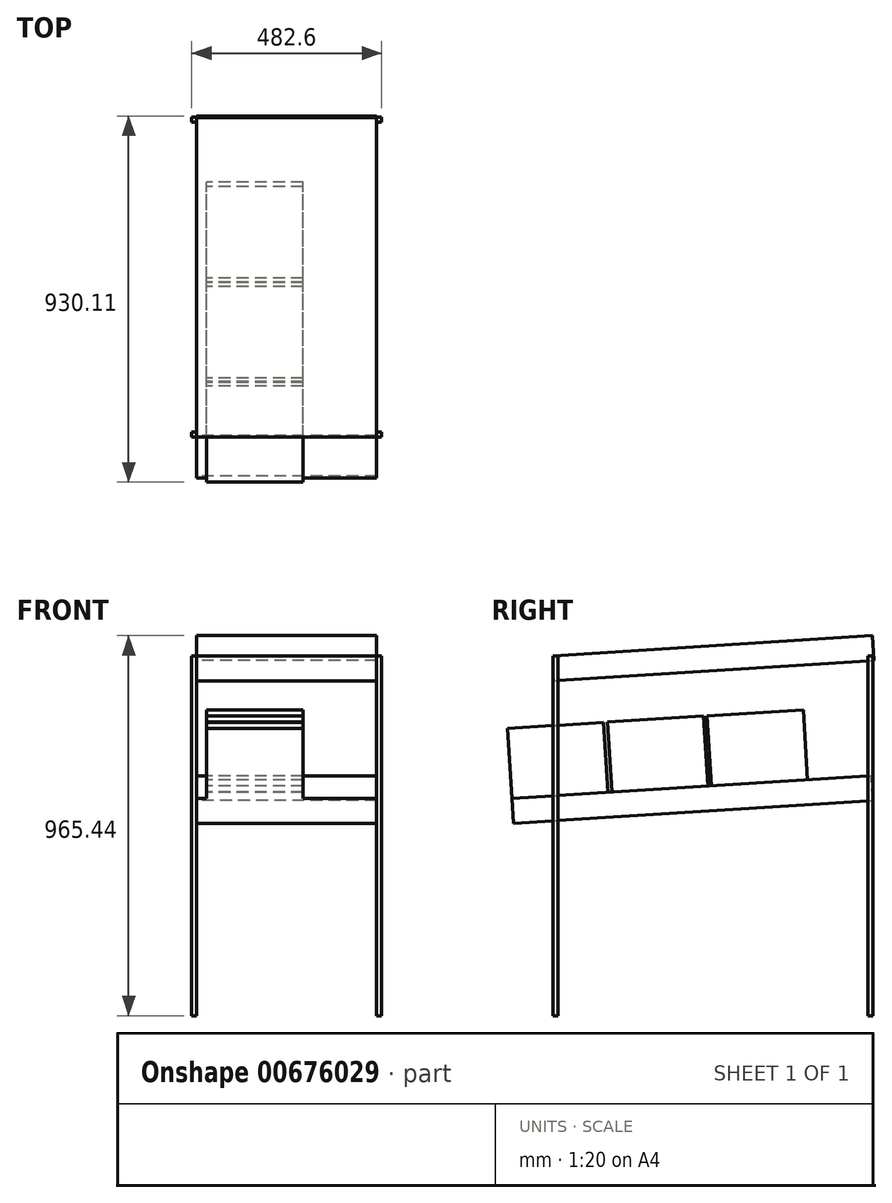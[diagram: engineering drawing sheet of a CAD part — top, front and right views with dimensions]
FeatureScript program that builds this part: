
annotation { "Feature Type Name" : "Feature", "Feature Type Description" : "" }
export const myFeature = defineFeature(function(context is Context, id is Id, definition is map)
    precondition{}
    {
        {
            var Q0;
            Q0=qCreatedBy(makeId("Top.planeOp"),FACE);
            cPlane(context, id + "F0", {"entities" : qUnion([Q0]), "cplaneType" : CPlaneType.OFFSET, "offset" : 558.8 * mm, "width" : 152.4 * mm, "height" : 152.4 * mm});
        }
        {
            var Q0;
            Q0=qCreatedBy(makeId("Top.planeOp"),FACE);
            cPlane(context, id + "F1", {"entities" : qUnion([Q0]), "cplaneType" : CPlaneType.OFFSET, "offset" : 914.4 * mm, "width" : 152.4 * mm, "height" : 152.4 * mm});
        }
        {
            var Q0;
            Q0=qCreatedBy(makeId("Top.planeOp"),FACE);
            var sketch = newSketch(context, id + "F2", { "sketchPlane" : qUnion([Q0])});
            skLineSegment(sketch, "E0.bottom", {"start": v(-228.6, 0) * mm, "end": v(-241.3, 0) * mm});
            skLineSegment(sketch, "E0.top", {"start": v(-228.6, 12.7) * mm, "end": v(-241.3, 12.7) * mm});
            skLineSegment(sketch, "E0.left", {"start": v(-228.6, 0) * mm, "end": v(-228.6, 12.7) * mm});
            skLineSegment(sketch, "E0.right", {"start": v(-241.3, 0) * mm, "end": v(-241.3, 12.7) * mm});
            skLineSegment(sketch, "E1.bottom", {"start": v(228.6, 0) * mm, "end": v(241.3, 0) * mm});
            skLineSegment(sketch, "E1.top", {"start": v(228.6, 12.7) * mm, "end": v(241.3, 12.7) * mm});
            skLineSegment(sketch, "E1.left", {"start": v(228.6, 0) * mm, "end": v(228.6, 12.7) * mm});
            skLineSegment(sketch, "E1.right", {"start": v(241.3, 0) * mm, "end": v(241.3, 12.7) * mm});
            skLineSegment(sketch, "E2.bottom", {"start": v(228.6, 800.1) * mm, "end": v(241.3, 800.1) * mm});
            skLineSegment(sketch, "E2.top", {"start": v(228.6, 812.8) * mm, "end": v(241.3, 812.8) * mm});
            skLineSegment(sketch, "E2.left", {"start": v(228.6, 800.1) * mm, "end": v(228.6, 812.8) * mm});
            skLineSegment(sketch, "E2.right", {"start": v(241.3, 800.1) * mm, "end": v(241.3, 812.8) * mm});
            skLineSegment(sketch, "E3.bottom", {"start": v(-228.6, 812.8) * mm, "end": v(-241.3, 812.8) * mm});
            skLineSegment(sketch, "E3.top", {"start": v(-228.6, 800.1) * mm, "end": v(-241.3, 800.1) * mm});
            skLineSegment(sketch, "E3.left", {"start": v(-228.6, 812.8) * mm, "end": v(-228.6, 800.1) * mm});
            skLineSegment(sketch, "E3.right", {"start": v(-241.3, 812.8) * mm, "end": v(-241.3, 800.1) * mm});
            skSolve(sketch);
        }
        {
            var Q0;
            Q0 = qSketchRegion(id + "F2", true);
            var Q1;
            Q1=qCreatedBy(id+"F1.planeOp",FACE);
            extrude(context, id + "F3", {"entities" : qUnion([Q0]), "endBound" : BoundingType.UP_TO_SURFACE, "depth" : 25.4 * mm, "endBoundEntityFace" : qUnion([Q1]), "offsetDistance" : 25.4 * mm});
        }
        {
            var Q0;
            Q0=qCreatedBy(id+"F0.planeOp",FACE);
            var sketch = newSketch(context, id + "F4", { "sketchPlane" : qUnion([Q0])});
            skLineSegment(sketch, "E4", {"start": v(-101.6, 0) * mm, "end": v(101.6, 0) * mm, "construction": true});
            skSolve(sketch);
        }
        {
            var Q0;
            Q0 = qBodyType(qCreatedBy(id + "F4" ,EDGE), BodyType.WIRE);
            var Q1;
            Q1=qCreatedBy(id+"F0.planeOp",FACE);
            cPlane(context, id + "F5", {"entities" : qUnion([Q0, Q1]), "cplaneType" : CPlaneType.LINE_ANGLE, "offset" : 25.4 * mm, "angle" : 3.6 * degree, "width" : 152.4 * mm, "height" : 152.4 * mm});
        }
        {
            var Q0;
            Q0=qCreatedBy(id+"F5.planeOp",FACE);
            var sketch = newSketch(context, id + "F6", { "sketchPlane" : qUnion([Q0])});
            skLineSegment(sketch, "E5.bottom", {"start": v(228.6, 68.88) * mm, "end": v(-228.6, 68.88) * mm});
            skLineSegment(sketch, "E5.top", {"start": v(228.6, -845.52) * mm, "end": v(-228.6, -845.52) * mm});
            skLineSegment(sketch, "E5.left", {"start": v(228.6, 68.88) * mm, "end": v(228.6, -845.52) * mm});
            skLineSegment(sketch, "E5.right", {"start": v(-228.6, 68.88) * mm, "end": v(-228.6, -845.52) * mm});
            skSolve(sketch);
        }
        {
            var Q0;
            Q0 = qSketchRegion(id + "F6", true);
            extrude(context, id + "F7", {"entities" : qUnion([Q0]), "depth" : 63.5 * mm, "offsetDistance" : 25.4 * mm});
        }
        {
            var Q0;
            Q0=qCreatedBy(id+"F1.planeOp",FACE);
            var sketch = newSketch(context, id + "F8", { "sketchPlane" : qUnion([Q0])});
            skLineSegment(sketch, "E6", {"start": v(102.97, 0) * mm, "end": v(-125.63, 0) * mm});
            skSolve(sketch);
        }
        {
            var Q0;
            Q0 = qBodyType(qCreatedBy(id + "F8" ,EDGE), BodyType.WIRE);
            var Q1;
            Q1=qCreatedBy(id+"F1.planeOp",FACE);
            cPlane(context, id + "F9", {"entities" : qUnion([Q0, Q1]), "cplaneType" : CPlaneType.LINE_ANGLE, "offset" : 25.4 * mm, "angle" : 3.6 * degree, "oppositeDirection" : true, "width" : 152.4 * mm, "height" : 152.4 * mm});
        }
        {
            var Q0;
            Q0=qCreatedBy(id+"F9.planeOp",FACE);
            var sketch = newSketch(context, id + "F10", { "sketchPlane" : qUnion([Q0])});
            skLineSegment(sketch, "E7.bottom", {"start": v(228.6, -57.42) * mm, "end": v(-228.6, -57.42) * mm});
            skLineSegment(sketch, "E7.top", {"start": v(228.6, -870.22) * mm, "end": v(-228.6, -870.22) * mm});
            skLineSegment(sketch, "E7.left", {"start": v(228.6, -57.42) * mm, "end": v(228.6, -870.22) * mm});
            skLineSegment(sketch, "E7.right", {"start": v(-228.6, -57.42) * mm, "end": v(-228.6, -870.22) * mm});
            skSolve(sketch);
        }
        {
            var Q0;
            Q0 = qSketchRegion(id + "F10", true);
            extrude(context, id + "F11", {"entities" : qUnion([Q0]), "depth" : 63.5 * mm, "offsetDistance" : 25.4 * mm});
        }
        {
            var Q0;
            Q0=qCreatedBy(id+"F5.planeOp",FACE);
            var sketch = newSketch(context, id + "F12", { "sketchPlane" : qUnion([Q0])});
            skLineSegment(sketch, "E8.bottom", {"start": v(41.27, 68.88) * mm, "end": v(-203.2, 68.88) * mm});
            skLineSegment(sketch, "E8.top", {"start": v(41.27, -175.6) * mm, "end": v(-203.2, -175.6) * mm});
            skLineSegment(sketch, "E8.left", {"start": v(41.27, 68.88) * mm, "end": v(41.28, -175.6) * mm});
            skLineSegment(sketch, "E8.right", {"start": v(-203.2, 68.88) * mm, "end": v(-203.2, -175.6) * mm});
            skLineSegment(sketch, "E9.0.1.0", {"start": v(41.28, -429.6) * mm, "end": v(-203.2, -429.6) * mm});
            skLineSegment(sketch, "E9.0.1.1", {"start": v(-203.2, -185.12) * mm, "end": v(-203.2, -429.6) * mm});
            skLineSegment(sketch, "E9.0.1.2", {"start": v(41.27, -185.12) * mm, "end": v(-203.2, -185.12) * mm});
            skLineSegment(sketch, "E9.0.1.3", {"start": v(41.27, -185.12) * mm, "end": v(41.28, -429.6) * mm});
            skLineSegment(sketch, "E9.0.2.0", {"start": v(41.28, -683.6) * mm, "end": v(-203.2, -683.6) * mm});
            skLineSegment(sketch, "E9.0.2.1", {"start": v(-203.2, -439.12) * mm, "end": v(-203.2, -683.6) * mm});
            skLineSegment(sketch, "E9.0.2.2", {"start": v(41.28, -439.12) * mm, "end": v(-203.2, -439.12) * mm});
            skLineSegment(sketch, "E9.0.2.3", {"start": v(41.27, -439.12) * mm, "end": v(41.28, -683.6) * mm});
            skLineSegment(sketch, "E9.direction1", {"start": v(-203.2, -175.6) * mm, "end": v(-203.2, -175.6) * mm});
            skLineSegment(sketch, "E9.direction2", {"start": v(-203.2, -175.6) * mm, "end": v(-203.2, -429.6) * mm, "construction": true});
            skSolve(sketch);
        }
        {
            var Q0;
            Q0 = qSketchRegion(id + "F12", true);
            extrude(context, id + "F13", {"entities" : qUnion([Q0]), "operationType" : NewBodyOperationType.ADD, "oppositeDirection" : true, "depth" : 177.8 * mm, "offsetDistance" : 25.4 * mm});
        }
        {
            var Q0;
            Q0=qCreatedBy(id+"F9.planeOp",FACE);
            var sketch = newSketch(context, id + "F14", { "sketchPlane" : qUnion([Q0])});
            skLineSegment(sketch, "E10.bottom", {"start": v(165.1, -57.42) * mm, "end": v(-165.1, -57.42) * mm});
            skLineSegment(sketch, "E10.top", {"start": v(165.1, -381.27) * mm, "end": v(-165.1, -381.27) * mm});
            skLineSegment(sketch, "E10.left", {"start": v(165.1, -57.42) * mm, "end": v(165.1, -381.27) * mm});
            skLineSegment(sketch, "E10.right", {"start": v(-165.1, -57.42) * mm, "end": v(-165.1, -381.27) * mm});
            skLineSegment(sketch, "E11.0.1.0", {"start": v(165.1, -730.52) * mm, "end": v(-165.1, -730.52) * mm});
            skLineSegment(sketch, "E11.0.1.1", {"start": v(-165.1, -406.67) * mm, "end": v(-165.1, -730.52) * mm});
            skLineSegment(sketch, "E11.0.1.2", {"start": v(165.1, -406.67) * mm, "end": v(-165.1, -406.67) * mm});
            skLineSegment(sketch, "E11.0.1.3", {"start": v(165.1, -406.67) * mm, "end": v(165.1, -730.52) * mm});
            skLineSegment(sketch, "E11.direction1", {"start": v(-165.1, -381.27) * mm, "end": v(-139.7, -381.27) * mm, "construction": true});
            skLineSegment(sketch, "E11.direction2", {"start": v(-165.1, -381.27) * mm, "end": v(-165.1, -730.52) * mm, "construction": true});
            skSolve(sketch);
        }
        {
            var Q0;
            Q0 = qConstructionFilter(qBodyType(qCreatedBy(id + "F14" ,EDGE), BodyType.WIRE), ConstructionObject.NO);
            extrude(context, id + "F15", {"bodyType" : ToolBodyType.SURFACE, "surfaceEntities" : qUnion([Q0]), "oppositeDirection" : true, "depth" : 196.85 * mm, "offsetDistance" : 25.4 * mm});
        }
    });
